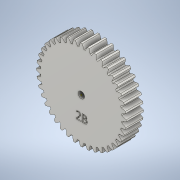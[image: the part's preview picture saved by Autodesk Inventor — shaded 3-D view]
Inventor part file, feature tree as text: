
AUTODESK INVENTOR PART (.ipt)
format: ipt  version: 2021 (Build 250183000, 183)  size: 400,896 bytes
history: native  units: mm (DEFAULTED — no unit token found)
features: sketch x5, plane x3, other x3, extrude x1, hole x1, emboss x1
ambient origin geometry x8: Origin, YZ Plane, XZ Plane, XY Plane, X Axis, Y Axis, Z Axis, Center Point
bodies: Solid1 (feature_tree)
feature tree (14):
  extrude  "Extrusion1"  Depth=8.0mm TaperAngle=0.0deg
  plane  "Work Plane2"
  plane  "Work Plane8"
  plane  "Work Plane9"
  other  "Spur Gear"
  sketch  "Sketch3"  dims[d16=25.351695mm]
  hole  "Hole1"  [1 undecoded]
  emboss  "Emboss1"
  sketch  "Sketch1"  dims[d0=41.564361mm d1=8.0mm d2=0.0mm]
  sketch  "Sketch2"  dims[d3=40.0mm d4=10.0mm d5=0.0mm]
  other  "Srf1"
  sketch  "Sketch4"  dims[d17=0.0mm d34=0.785398mm]
  sketch  "Sketch5"  dims[d39=0.0mm d41=0.0mm d43=25.351695mm d46=25.351695mm d47=0.0mm d48=0.0mm d49=3.0mm d50=3.0mm d51=6.0mm d52=4.0mm d53=2.0mm d54=90.0deg d55=8.0mm d56=20.594885mm d57=1.0mm d58=0.0mm]
  other  "Pitch Diameter"
note: 1 required parameter value undecoded (feature->parameter linkage not recoverable at this tier; creation-order binding heuristic only, values carry confidence <= 0.55)
